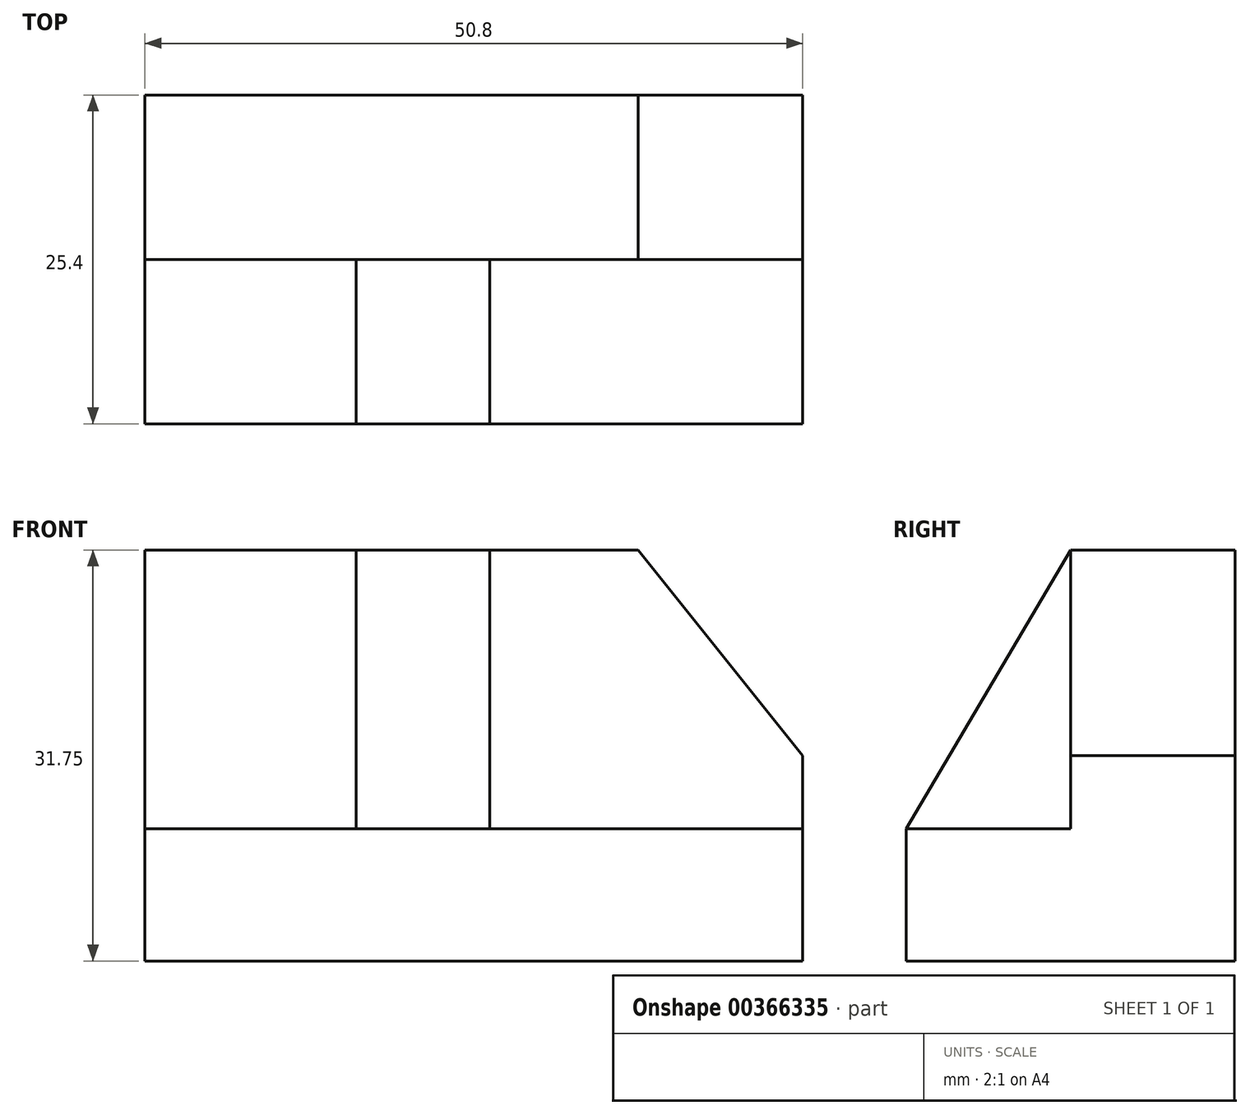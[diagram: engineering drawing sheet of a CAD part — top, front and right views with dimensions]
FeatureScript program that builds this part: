
annotation { "Feature Type Name" : "Feature", "Feature Type Description" : "" }
export const myFeature = defineFeature(function(context is Context, id is Id, definition is map)
    precondition{}
    {
        {
            var Q0;
            Q0=qCreatedBy(makeId("Front.planeOp"),FACE);
            var sketch = newSketch(context, id + "F0", { "sketchPlane" : qUnion([Q0])});
            skLineSegment(sketch, "E0", {"start": v(0, 0) * mm, "end": v(50.8, 0) * mm});
            skLineSegment(sketch, "E1", {"start": v(50.8, 0) * mm, "end": v(50.8, 31.75) * mm});
            skLineSegment(sketch, "E2", {"start": v(50.8, 31.75) * mm, "end": v(0, 31.75) * mm});
            skLineSegment(sketch, "E3", {"start": v(0, 31.75) * mm, "end": v(0, 0) * mm});
            skSolve(sketch);
        }
        {
            var Q0;
            Q0=makeQuery(id+"F0.imprint","IMPRINT",FACE,{"disambiguationData":[TD([[makeQuery(id+"F0.imprint","IMPRINT",EDGE,{"derivedFrom":sQuery(id+"F0.wireOp",EDGE,"E0")}),1.0]])]});
            extrude(context, id + "F1", {"entities" : qUnion([Q0]), "depth" : 25.4 * mm});
        }
        {
            var Q0;
            Q0=makeQuery(id+"F1.opExtrude","CAP_FACE",FACE,{"disambiguationData":[OSD([sQuery(id+"F0.wireOp",EDGE,"E0"),sQuery(id+"F0.wireOp",EDGE,"E1"),sQuery(id+"F0.wireOp",EDGE,"E2"),sQuery(id+"F0.wireOp",EDGE,"E3")])],"isStart":true});
            var sketch = newSketch(context, id + "F2", { "sketchPlane" : qUnion([Q0])});
            skLineSegment(sketch, "E4", {"start": v(-50.8, 15.87) * mm, "end": v(-38.1, 31.75) * mm});
            skLineSegment(sketch, "E5", {"start": v(-50.8, 15.88) * mm, "end": v(-50.8, 31.75) * mm});
            skLineSegment(sketch, "E6", {"start": v(-50.8, 31.75) * mm, "end": v(-38.1, 31.75) * mm});
            skSolve(sketch);
        }
        {
            var Q0;
            Q0=makeQuery(id+"F2.imprint","IMPRINT",FACE,{"disambiguationData":[TD([[makeQuery(id+"F2.imprint","IMPRINT",EDGE,{"derivedFrom":sQuery(id+"F2.wireOp",EDGE,"E4")}),1.0]])]});
            extrude(context, id + "F3", {"entities" : qUnion([Q0]), "operationType" : NewBodyOperationType.REMOVE, "oppositeDirection" : true, "depth" : 12.7 * mm});
        }
        {
            var Q0;
            Q0=makeQuery(id+"F1.opExtrude","CAP_FACE",FACE,{"disambiguationData":[OSD([sQuery(id+"F0.wireOp",EDGE,"E0"),sQuery(id+"F0.wireOp",EDGE,"E1"),sQuery(id+"F0.wireOp",EDGE,"E2"),sQuery(id+"F0.wireOp",EDGE,"E3")])],"isStart":false});
            var sketch = newSketch(context, id + "F4", { "sketchPlane" : qUnion([Q0])});
            skLineSegment(sketch, "E7", {"start": v(0, 10.21) * mm, "end": v(50.8, 10.21) * mm});
            skLineSegment(sketch, "E8", {"start": v(0, 10.21) * mm, "end": v(0, 0) * mm});
            skLineSegment(sketch, "E9", {"start": v(0, 0) * mm, "end": v(50.8, 0) * mm});
            skLineSegment(sketch, "E10", {"start": v(50.9, -0.94) * mm, "end": v(50.8, 10.21) * mm});
            skSolve(sketch);
        }
        {
            var Q0;
            Q0 = qSketchRegion(id + "F4", true);
            var Q1;
            {var subQ0=sQuery(id+"F4.wireOp",EDGE,"E7");Q1=makeQuery(id+"F4.imprint","IMPRINT",FACE,{"disambiguationData":[TD([[makeQuery(id+"F4.imprint","IMPRINT",EDGE,{"derivedFrom":subQ0}),1.0]])]});}
            extrude(context, id + "F5", {"entities" : qUnion([Q0, Q1]), "operationType" : NewBodyOperationType.REMOVE, "oppositeDirection" : true, "depth" : 12.7 * mm});
        }
        {
            var Q0;
            Q0=makeQuery(id+"F5.boolean.opBoolean","COPY",FACE,{"derivedFrom":makeQuery(id+"F5.opExtrude","CAP_FACE",FACE,{"disambiguationData":[OSD([sQuery(id+"F0.wireOp",EDGE,"E1"),sQuery(id+"F0.wireOp",EDGE,"E2"),sQuery(id+"F0.wireOp",EDGE,"E3"),sQuery(id+"F4.wireOp",EDGE,"E7")])],"isStart":false})});
            var sketch = newSketch(context, id + "F6", { "sketchPlane" : qUnion([Q0])});
            skLineSegment(sketch, "E11", {"start": v(16.31, 31.75) * mm, "end": v(16.31, 10.21) * mm});
            skLineSegment(sketch, "E12", {"start": v(26.64, 31.75) * mm, "end": v(26.64, 10.21) * mm});
            skSolve(sketch);
        }
        {
            var Q0;
            Q0 = qSketchRegion(id + "F6", true);
            var Q1;
            {var subQ0=sQuery(id+"F6.wireOp",EDGE,"E11");Q1=makeQuery(id+"F6.imprint","IMPRINT",FACE,{"disambiguationData":[TD([[makeQuery(id+"F6.imprint","IMPRINT",EDGE,{"derivedFrom":subQ0}),1.0]])]});}
            extrude(context, id + "F7", {"entities" : qUnion([Q0, Q1]), "operationType" : NewBodyOperationType.ADD, "depth" : 25.4 * mm});
        }
        {
            var Q0;
            Q0=makeQuery(id+"F7.opExtrude","SWEPT_FACE",FACE,{"disambiguationData":[OSD([sQuery(id+"F6.wireOp",EDGE,"E11")])]});
            var sketch = newSketch(context, id + "F8", { "sketchPlane" : qUnion([Q0])});
            skLineSegment(sketch, "E13", {"start": v(12.7, 31.75) * mm, "end": v(25.4, 10.21) * mm});
            skSolve(sketch);
        }
        {
            var Q0;
            Q0 = qSketchRegion(id + "F8", true);
            var Q1;
            Q1=makeQuery(id+"F8.imprint","IMPRINT",FACE,{"disambiguationData":[TD([[makeQuery(id+"F8.imprint","IMPRINT",EDGE,{"derivedFrom":sQuery(id+"F8.wireOp",EDGE,"E13")}),1.0]])]});
            extrude(context, id + "F9", {"entities" : qUnion([Q0, Q1]), "operationType" : NewBodyOperationType.REMOVE, "oppositeDirection" : true, "depth" : 25.4 * mm});
        }
    });
